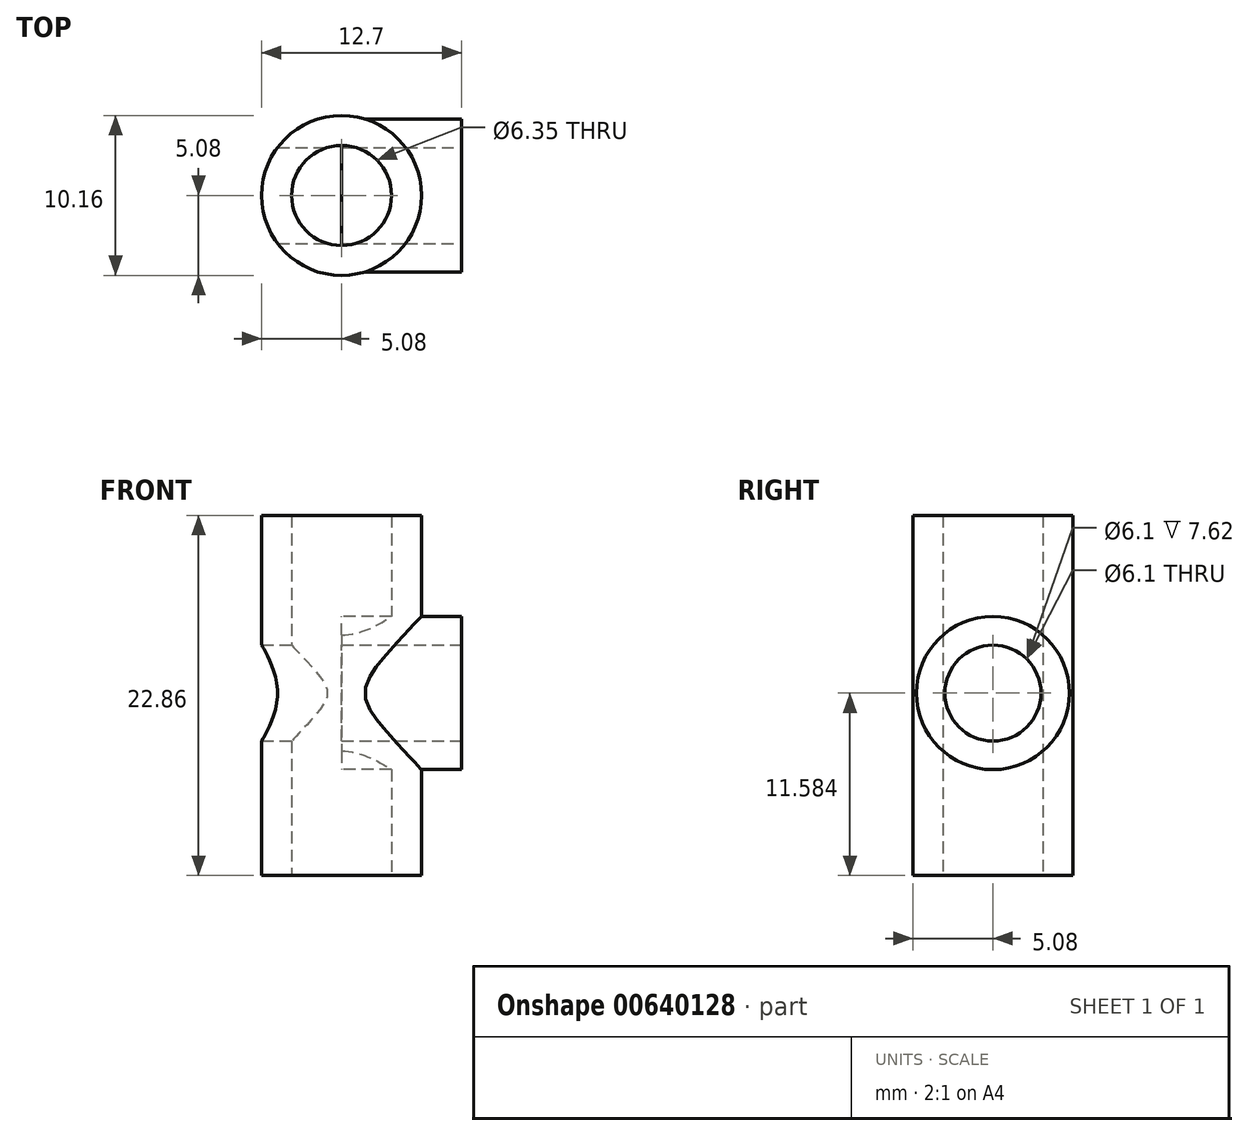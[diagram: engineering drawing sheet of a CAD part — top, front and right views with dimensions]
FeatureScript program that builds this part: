
annotation { "Feature Type Name" : "Feature", "Feature Type Description" : "" }
export const myFeature = defineFeature(function(context is Context, id is Id, definition is map)
    precondition{}
    {
        {
            var Q0;
            Q0=qCreatedBy(makeId("Top.planeOp"),FACE);
            var sketch = newSketch(context, id + "F0", { "sketchPlane" : qUnion([Q0])});
            skCircle(sketch, "E0", {"center": v(0, 0) * mm, "radius": 5.08 * mm});
            skSolve(sketch);
        }
        {
            var Q0;
            Q0 = qSketchRegion(id + "F0", true);
            extrude(context, id + "F1", {"entities" : qUnion([Q0]), "depth" : 22.86 * mm, "offsetDistance" : 25.4 * mm});
        }
        {
            var Q0;
            Q0=makeQuery(id+"F1.opExtrude","CAP_FACE",FACE,{"disambiguationData":[OSD([sQuery(id+"F0.wireOp",EDGE,"E0")])],"isStart":true});
            var sketch = newSketch(context, id + "F2", { "sketchPlane" : qUnion([Q0])});
            skCircle(sketch, "E1", {"center": v(0, 0) * mm, "radius": 3.18 * mm});
            skSolve(sketch);
        }
        {
            var Q0;
            Q0=sQuery(id+"F2.wireOp",VERTEX,"E1.center");
            var Q1;
            Q1=makeQuery(id+"F1.opExtrude","SWEPT_BODY",BODY,{"disambiguationData":[OSD([sQuery(id+"F0.wireOp",EDGE,"E0")])]});
            hole(context, id + "F3", {"style" : HoleStyle.SIMPLE, "endStyle" : HoleEndStyle.THROUGH, "holeDiameter" : 6.35 * mm, "majorDiameter" : 6.35 * mm, "isTappedThrough" : true, "tappedDepth" : 12.7 * mm, "tapClearance" : 3, "locations" : qUnion([Q0]), "scope" : qUnion([Q1])});
        }
        {
            var Q0;
            Q0=qCreatedBy(makeId("Right.planeOp"),FACE);
            var sketch = newSketch(context, id + "F4", { "sketchPlane" : qUnion([Q0])});
            skCircle(sketch, "E2", {"center": v(0, 11.58) * mm, "radius": 4.86 * mm});
            skSolve(sketch);
        }
        {
            var Q0;
            Q0 = qSketchRegion(id + "F4", true);
            extrude(context, id + "F5", {"entities" : qUnion([Q0]), "operationType" : NewBodyOperationType.ADD, "depth" : 7.62 * mm, "offsetDistance" : 25.4 * mm});
        }
        {
            var Q0;
            Q0=makeQuery(id+"F5.opExtrude","CAP_FACE",FACE,{"disambiguationData":[OSD([sQuery(id+"F4.wireOp",EDGE,"E2")])],"isStart":false});
            var sketch = newSketch(context, id + "F6", { "sketchPlane" : qUnion([Q0])});
            skCircle(sketch, "E3", {"center": v(0, 11.58) * mm, "radius": 3.14 * mm});
            skSolve(sketch);
        }
        {
            var Q0;
            Q0=sQuery(id+"F6.wireOp",VERTEX,"E3.center");
            var Q1;
            Q1=makeQuery(id+"F1.opExtrude","SWEPT_BODY",BODY,{"disambiguationData":[OSD([sQuery(id+"F0.wireOp",EDGE,"E0")])]});
            hole(context, id + "F7", {"style" : HoleStyle.SIMPLE, "endStyle" : HoleEndStyle.THROUGH, "holeDiameter" : 6.1 * mm, "majorDiameter" : 6.35 * mm, "isTappedThrough" : true, "tappedDepth" : 12.7 * mm, "tapClearance" : 3, "locations" : qUnion([Q0]), "scope" : qUnion([Q1])});
        }
    });
